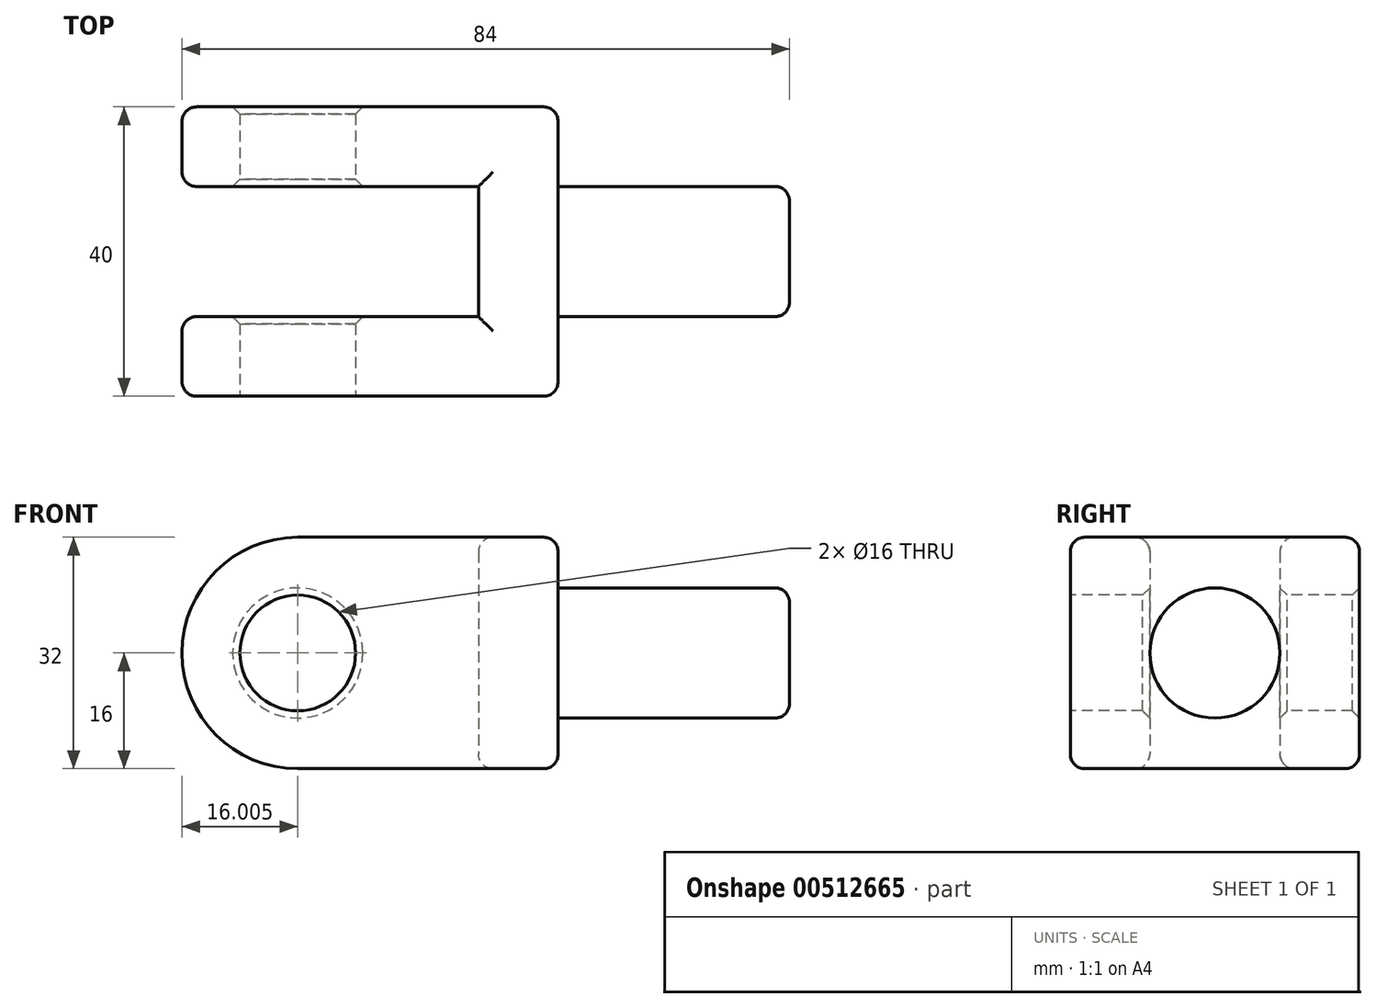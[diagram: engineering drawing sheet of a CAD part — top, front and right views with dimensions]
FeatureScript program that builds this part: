
annotation { "Feature Type Name" : "Feature", "Feature Type Description" : "" }
export const myFeature = defineFeature(function(context is Context, id is Id, definition is map)
    precondition{}
    {
        {
            var Q0;
            Q0=qCreatedBy(makeId("Front.planeOp"),FACE);
            var sketch = newSketch(context, id + "F0", { "sketchPlane" : qUnion([Q0])});
            skLineSegment(sketch, "E0", {"start": v(0, -56.18) * mm, "end": v(0, 37.47) * mm, "construction": true});
            skLineSegment(sketch, "E1", {"start": v(-60.47, 0) * mm, "end": v(78.3, 0) * mm, "construction": true});
            skLineSegment(sketch, "E2", {"start": v(22.62, 16) * mm, "end": v(22.62, -16) * mm});
            skLineSegment(sketch, "E3", {"start": v(22.62, -16) * mm, "end": v(-13.38, -16) * mm});
            skLineSegment(sketch, "E4", {"start": v(22.62, 16) * mm, "end": v(-13.38, 16) * mm});
            skArc(sketch, "E5", {"start": v(-13.38, -16) * mm, "mid": v(-29.38, 0) * mm, "end": v(-13.38, 16) * mm});
            skSolve(sketch);
        }
        {
            var Q0;
            Q0 = qSketchRegion(id + "F0", true);
            extrude(context, id + "F1", {"entities" : qUnion([Q0]), "depth" : 20 * mm, "offsetDistance" : 25 * mm, "hasSecondDirection" : true, "secondDirectionOppositeDirection" : true, "secondDirectionDepth" : 20 * mm});
        }
        {
            var Q0;
            Q0=makeQuery(id+"F1.opExtrude","CAP_FACE",FACE,{"disambiguationData":[OSD([sQuery(id+"F0.wireOp",EDGE,"E2"),sQuery(id+"F0.wireOp",EDGE,"E3"),sQuery(id+"F0.wireOp",EDGE,"E4"),sQuery(id+"F0.wireOp",EDGE,"E5")])],"isStart":false});
            var sketch = newSketch(context, id + "F2", { "sketchPlane" : qUnion([Q0])});
            skCircle(sketch, "E6", {"center": v(-13.38, 0) * mm, "radius": 8 * mm});
            skSolve(sketch);
        }
        {
            var Q0;
            Q0 = qSketchRegion(id + "F2", true);
            extrude(context, id + "F3", {"entities" : qUnion([Q0]), "operationType" : NewBodyOperationType.REMOVE, "endBound" : BoundingType.THROUGH_ALL, "oppositeDirection" : true, "depth" : 25 * mm, "offsetDistance" : 25 * mm});
        }
        {
            var Q0;
            Q0=qCreatedBy(makeId("Top.planeOp"),FACE);
            var sketch = newSketch(context, id + "F4", { "sketchPlane" : qUnion([Q0])});
            skPoint(sketch, "E7.middle", {"position": v(0, 0) * mm});
            skLineSegment(sketch, "E8.bottom", {"start": v(11.62, -9) * mm, "end": v(-50.92, -9) * mm});
            skLineSegment(sketch, "E8.top", {"start": v(11.62, 9) * mm, "end": v(-50.92, 9) * mm});
            skLineSegment(sketch, "E8.left", {"start": v(11.62, -9) * mm, "end": v(11.62, 9) * mm});
            skLineSegment(sketch, "E8.right", {"start": v(-50.92, -9) * mm, "end": v(-50.92, 9) * mm});
            skSolve(sketch);
        }
        {
            var Q0;
            Q0 = qSketchRegion(id + "F4", true);
            extrude(context, id + "F5", {"entities" : qUnion([Q0]), "operationType" : NewBodyOperationType.REMOVE, "endBound" : BoundingType.THROUGH_ALL, "depth" : 25 * mm, "offsetDistance" : 25 * mm, "hasSecondDirection" : true, "secondDirectionOppositeDirection" : true, "secondDirectionDepth" : 25 * mm});
        }
        {
            var Q0;
            Q0=makeQuery(id+"F1.opExtrude","SWEPT_FACE",FACE,{"disambiguationData":[OSD([sQuery(id+"F0.wireOp",EDGE,"E2")])]});
            var sketch = newSketch(context, id + "F6", { "sketchPlane" : qUnion([Q0])});
            skCircle(sketch, "E9", {"center": v(0, 0) * mm, "radius": 9 * mm});
            skSolve(sketch);
        }
        {
            var Q0;
            Q0 = qSketchRegion(id + "F6", true);
            extrude(context, id + "F7", {"entities" : qUnion([Q0]), "operationType" : NewBodyOperationType.ADD, "depth" : 32 * mm, "offsetDistance" : 25 * mm});
        }
        {
            var Q0;
            Q0=makeQuery(id+"F3.boolean.opBoolean","COPY",EDGE,{"derivedFrom":makeQuery(id+"F3.opExtrude","CAP_EDGE",EDGE,{"disambiguationData":[OSD([sQuery(id+"F2.wireOp",EDGE,"E6")])],"isStart":true})});
            var Q1;
            Q1=makeQuery(id+"F3.boolean.opBoolean","INTERSECT",EDGE,{"derivedFrom":[makeQuery(id+"F1.opExtrude","CAP_FACE",FACE,{"disambiguationData":[OSD([sQuery(id+"F0.wireOp",EDGE,"E2"),sQuery(id+"F0.wireOp",EDGE,"E3"),sQuery(id+"F0.wireOp",EDGE,"E4"),sQuery(id+"F0.wireOp",EDGE,"E5")])],"isStart":true}),makeQuery(id+"F3.opExtrude","SWEPT_FACE",FACE,{"disambiguationData":[OSD([sQuery(id+"F2.wireOp",EDGE,"E6")])]})]});
            var Q2;
            Q2=makeQuery(id+"F5.boolean.opBoolean","INTERSECT",EDGE,{"derivedFrom":[makeQuery(id+"F3.boolean.opBoolean","COPY",FACE,{"derivedFrom":makeQuery(id+"F3.opExtrude","SWEPT_FACE",FACE,{"disambiguationData":[OSD([sQuery(id+"F2.wireOp",EDGE,"E6")])]})}),makeQuery(id+"F5.opExtrude","SWEPT_FACE",FACE,{"disambiguationData":[OSD([sQuery(id+"F4.wireOp",EDGE,"E8.bottom")])]})]});
            var Q3;
            Q3=makeQuery(id+"F5.boolean.opBoolean","INTERSECT",EDGE,{"derivedFrom":[makeQuery(id+"F3.boolean.opBoolean","COPY",FACE,{"derivedFrom":makeQuery(id+"F3.opExtrude","SWEPT_FACE",FACE,{"disambiguationData":[OSD([sQuery(id+"F2.wireOp",EDGE,"E6")])]})}),makeQuery(id+"F5.opExtrude","SWEPT_FACE",FACE,{"disambiguationData":[OSD([sQuery(id+"F4.wireOp",EDGE,"E8.top")])]})]});
            chamfer(context, id + "F8", {"entities" : qUnion([Q0, Q1, Q2, Q3]), "width" : 1 * mm, "tangentPropagation" : true});
        }
        {
            var Q0;
            Q0=makeQuery(id+"F1.opExtrude","CAP_EDGE",EDGE,{"disambiguationData":[OSD([sQuery(id+"F0.wireOp",EDGE,"E5")])],"isStart":false});
            var Q1;
            Q1=makeQuery(id+"F5.boolean.opBoolean","INTERSECT",EDGE,{"derivedFrom":[makeQuery(id+"F1.opExtrude","SWEPT_FACE",FACE,{"disambiguationData":[OSD([sQuery(id+"F0.wireOp",EDGE,"E4")])]}),makeQuery(id+"F5.opExtrude","SWEPT_FACE",FACE,{"disambiguationData":[OSD([sQuery(id+"F4.wireOp",EDGE,"E8.bottom")])]})]});
            var Q2;
            Q2=makeQuery(id+"F5.boolean.opBoolean","INTERSECT",EDGE,{"derivedFrom":[makeQuery(id+"F1.opExtrude","SWEPT_FACE",FACE,{"disambiguationData":[OSD([sQuery(id+"F0.wireOp",EDGE,"E4")])]}),makeQuery(id+"F5.opExtrude","SWEPT_FACE",FACE,{"disambiguationData":[OSD([sQuery(id+"F4.wireOp",EDGE,"E8.left")])]})]});
            var Q3;
            Q3=makeQuery(id+"F5.boolean.opBoolean","INTERSECT",EDGE,{"derivedFrom":[makeQuery(id+"F1.opExtrude","SWEPT_FACE",FACE,{"disambiguationData":[OSD([sQuery(id+"F0.wireOp",EDGE,"E3")])]}),makeQuery(id+"F5.opExtrude","SWEPT_FACE",FACE,{"disambiguationData":[OSD([sQuery(id+"F4.wireOp",EDGE,"E8.left")])]})]});
            var Q4;
            Q4=makeQuery(id+"F5.boolean.opBoolean","INTERSECT",EDGE,{"derivedFrom":[makeQuery(id+"F1.opExtrude","SWEPT_FACE",FACE,{"disambiguationData":[OSD([sQuery(id+"F0.wireOp",EDGE,"E3")])]}),makeQuery(id+"F5.opExtrude","SWEPT_FACE",FACE,{"disambiguationData":[OSD([sQuery(id+"F4.wireOp",EDGE,"E8.top")])]})]});
            var Q5;
            Q5=makeQuery(id+"F1.opExtrude","CAP_EDGE",EDGE,{"disambiguationData":[OSD([sQuery(id+"F0.wireOp",EDGE,"E5")])],"isStart":true});
            var Q6;
            Q6=makeQuery(id+"F1.opExtrude","CAP_EDGE",EDGE,{"disambiguationData":[OSD([sQuery(id+"F0.wireOp",EDGE,"E2")])],"isStart":true});
            var Q7;
            Q7=makeQuery(id+"F1.opExtrude","SWEPT_EDGE",EDGE,{"disambiguationData":[OSD([sQuery(id+"F0.wireOp",EDGE,"E2"),sQuery(id+"F0.wireOp",EDGE,"E4")])]});
            var Q8;
            Q8=makeQuery(id+"F1.opExtrude","CAP_EDGE",EDGE,{"disambiguationData":[OSD([sQuery(id+"F0.wireOp",EDGE,"E2")])],"isStart":false});
            var Q9;
            Q9=makeQuery(id+"F1.opExtrude","SWEPT_EDGE",EDGE,{"disambiguationData":[OSD([sQuery(id+"F0.wireOp",EDGE,"E2"),sQuery(id+"F0.wireOp",EDGE,"E3")])]});
            var Q10;
            Q10=makeQuery(id+"F7.opExtrude","CAP_EDGE",EDGE,{"disambiguationData":[OSD([sQuery(id+"F6.wireOp",EDGE,"E9")])],"isStart":false});
            var Q11;
            Q11=makeQuery(id+"F7.opExtrude","CAP_EDGE",EDGE,{"disambiguationData":[OSD([sQuery(id+"F6.wireOp",EDGE,"E9")])],"isStart":true});
            fillet(context, id + "F9", {"entities" : qUnion([Q0, Q1, Q2, Q3, Q4, Q5, Q6, Q7, Q8, Q9, Q10, Q11]), "radius" : 2 * mm, "tangentPropagation" : true, "allowEdgeOverflow" : false});
        }
    });
